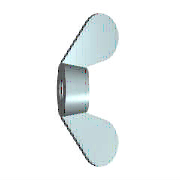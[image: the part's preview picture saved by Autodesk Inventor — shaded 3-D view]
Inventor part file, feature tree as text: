
AUTODESK INVENTOR PART (.ipt)
format: ipt  version: 2011 SP1 (Build 150282100, 282)  size: 169,984 bytes
history: native  units: mm (DEFAULTED — no unit token found)
features: extrude x1, mirror x1, hole x1, other x1, plane x1
ambient origin geometry x7: Origin, YZ Plane, XZ Plane, X Axis, Y Axis, Z Axis, Center Point
bodies: Solid1 (feature_tree), Body (feature_tree)
feature tree (5):
  extrude  "Wing1"  Depth=14.986mm
  mirror  "Wing2"
  hole  "Thread"  [1 undecoded]
  other  "Work Axis1"
  plane  "Work Plane1"
note: 1 required parameter value undecoded (feature->parameter linkage not recoverable at this tier; creation-order binding heuristic only, values carry confidence <= 0.55)
